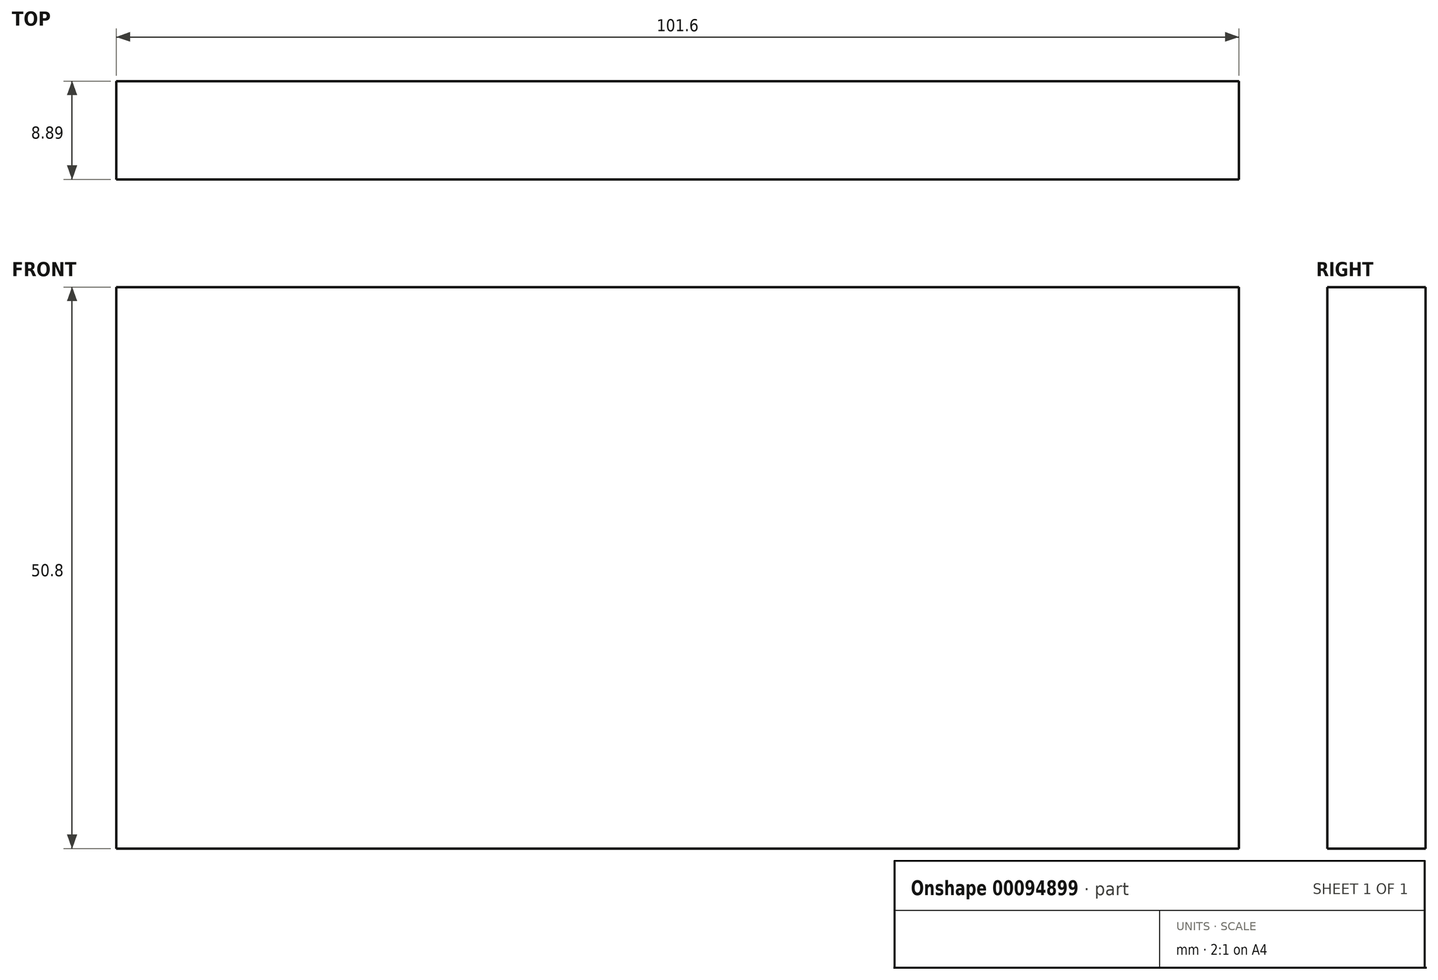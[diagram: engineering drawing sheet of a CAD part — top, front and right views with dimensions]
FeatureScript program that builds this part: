
annotation { "Feature Type Name" : "Feature", "Feature Type Description" : "" }
export const myFeature = defineFeature(function(context is Context, id is Id, definition is map)
    precondition{}
    {
        {
            var Q0;
            Q0=qCreatedBy(makeId("Front.planeOp"),FACE);
            var sketch = newSketch(context, id + "F0", { "sketchPlane" : qUnion([Q0])});
            skLineSegment(sketch, "E0", {"start": v(0, 0) * mm, "end": v(101.6, 0) * mm});
            skLineSegment(sketch, "E1", {"start": v(101.6, 0) * mm, "end": v(101.6, 50.8) * mm});
            skLineSegment(sketch, "E2", {"start": v(101.6, 50.8) * mm, "end": v(0, 50.8) * mm});
            skLineSegment(sketch, "E3", {"start": v(0, 50.8) * mm, "end": v(0, 0) * mm});
            skSolve(sketch);
        }
        {
            var Q0;
            Q0 = qSketchRegion(id + "F0", true);
            extrude(context, id + "F1", {"entities" : qUnion([Q0]), "depth" : 8.9 * mm});
        }
    });
